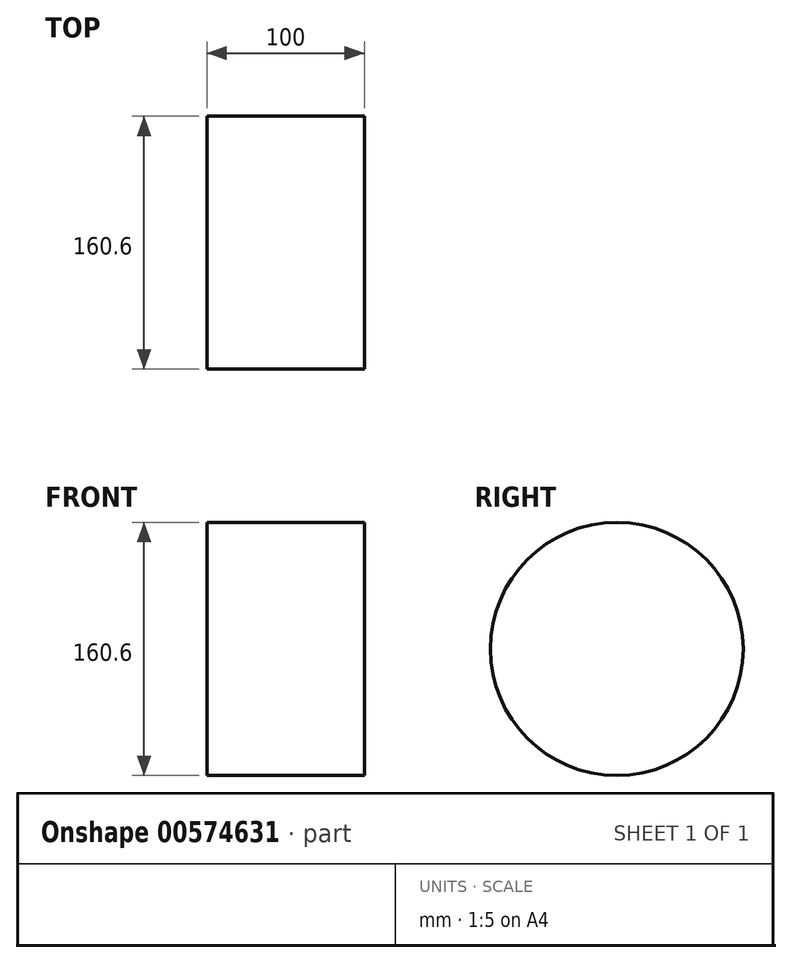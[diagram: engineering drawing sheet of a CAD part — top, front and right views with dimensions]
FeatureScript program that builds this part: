
annotation { "Feature Type Name" : "Feature", "Feature Type Description" : "" }
export const myFeature = defineFeature(function(context is Context, id is Id, definition is map)
    precondition{}
    {
        {
            var Q0;
            Q0=qCreatedBy(makeId("Right.planeOp"),FACE);
            var sketch = newSketch(context, id + "F0", { "sketchPlane" : qUnion([Q0])});
            skCircle(sketch, "E0", {"center": v(0, 0) * mm, "radius": 80.3 * mm});
            skSolve(sketch);
        }
        {
            var Q0;
            Q0=makeQuery(id+"F0.imprint","IMPRINT",FACE,{"disambiguationData":[TD([[makeQuery(id+"F0.imprint","IMPRINT",EDGE,{"derivedFrom":sQuery(id+"F0.wireOp",EDGE,"E0")}),1.0]])]});
            extrude(context, id + "F1", {"entities" : qUnion([Q0]), "depth" : 100 * mm, "offsetDistance" : 25.4 * mm});
        }
    });
